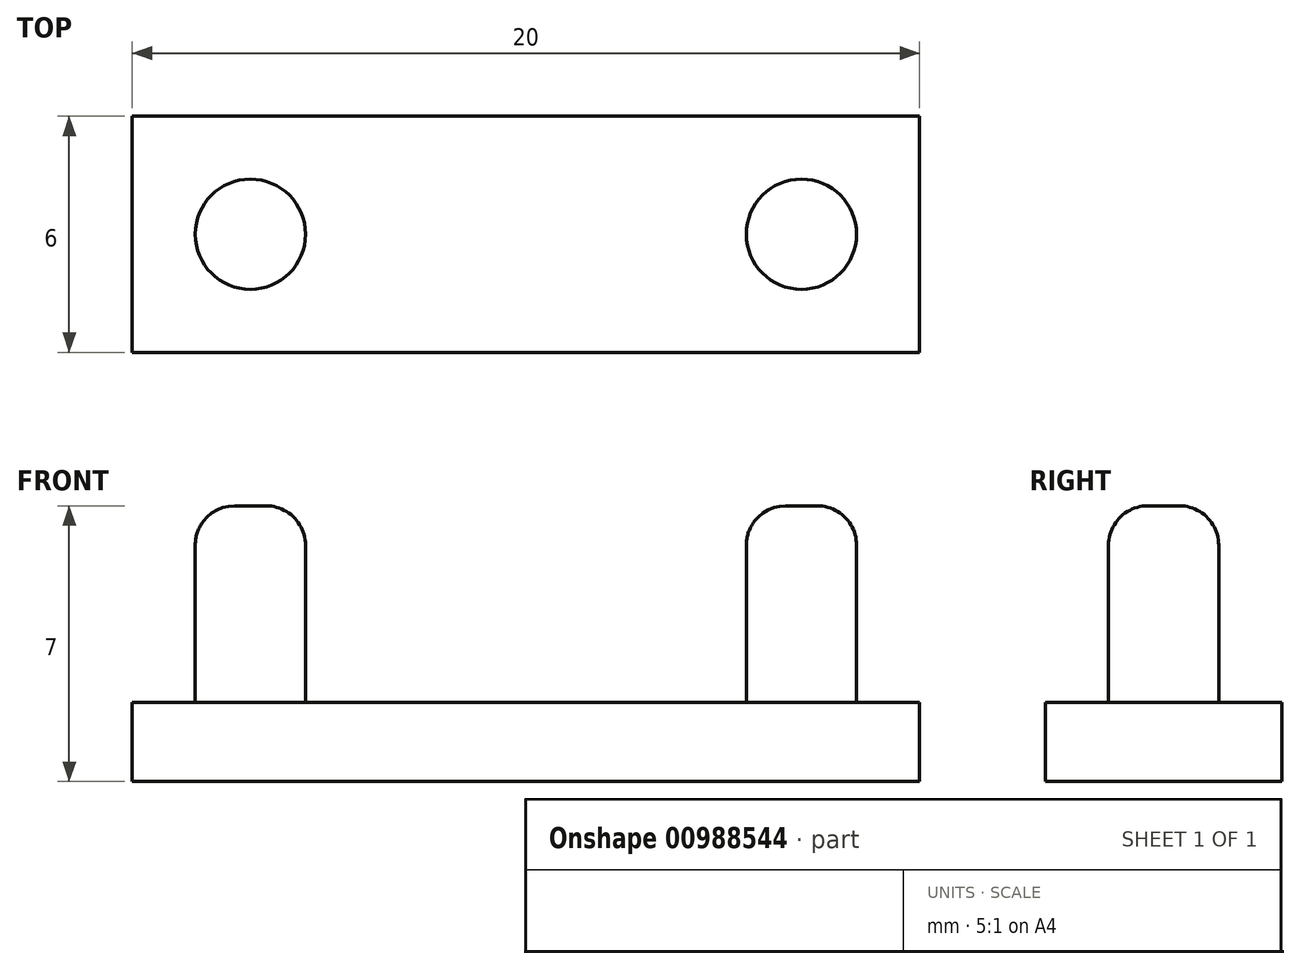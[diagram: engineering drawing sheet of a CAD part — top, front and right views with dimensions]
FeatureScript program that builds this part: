
annotation { "Feature Type Name" : "Feature", "Feature Type Description" : "" }
export const myFeature = defineFeature(function(context is Context, id is Id, definition is map)
    precondition{}
    {
        {
            var Q0;
            Q0=qCreatedBy(makeId("Top.planeOp"),FACE);
            var sketch = newSketch(context, id + "F0", { "sketchPlane" : qUnion([Q0])});
            skLineSegment(sketch, "E0.bottom", {"start": v(-10, 3) * mm, "end": v(10, 3) * mm});
            skLineSegment(sketch, "E0.top", {"start": v(-10, -3) * mm, "end": v(10, -3) * mm});
            skLineSegment(sketch, "E0.left", {"start": v(-10, 3) * mm, "end": v(-10, -3) * mm});
            skLineSegment(sketch, "E0.right", {"start": v(10, 3) * mm, "end": v(10, -3) * mm});
            skPoint(sketch, "E0.middle", {"position": v(0, 0) * mm});
            skPoint(sketch, "E1", {"position": v(-7, 0) * mm});
            skPoint(sketch, "E2", {"position": v(7, 0) * mm});
            skSolve(sketch);
        }
        {
            var Q0;
            Q0=makeQuery(id+"F0.imprint","IMPRINT",FACE,{"disambiguationData":[TD([[makeQuery(id+"F0.imprint","IMPRINT",EDGE,{"derivedFrom":sQuery(id+"F0.wireOp",EDGE,"E0.bottom")}),-1.0]])]});
            extrude(context, id + "F1", {"entities" : qUnion([Q0]), "depth" : 2 * mm, "offsetDistance" : 25 * mm});
        }
        {
            var Q0;
            Q0=makeQuery(id+"F1.opExtrude","CAP_FACE",FACE,{"disambiguationData":[OSD([sQuery(id+"F0.wireOp",EDGE,"E0.bottom"),sQuery(id+"F0.wireOp",EDGE,"E0.top"),sQuery(id+"F0.wireOp",EDGE,"E0.left"),sQuery(id+"F0.wireOp",EDGE,"E0.right")])],"isStart":false});
            var sketch = newSketch(context, id + "F2", { "sketchPlane" : qUnion([Q0])});
            skPoint(sketch, "E3", {"position": v(-7, 0) * mm});
            skPoint(sketch, "E4", {"position": v(7, 0) * mm});
            skCircle(sketch, "E5", {"center": v(-7, 0) * mm, "radius": 1.4 * mm});
            skCircle(sketch, "E6", {"center": v(7, 0) * mm, "radius": 1.4 * mm});
            skSolve(sketch);
        }
        {
            var Q0;
            Q0=makeQuery(id+"F2.imprint","IMPRINT",FACE,{"disambiguationData":[TD([[makeQuery(id+"F2.imprint","IMPRINT",EDGE,{"derivedFrom":sQuery(id+"F2.wireOp",EDGE,"E5")}),1.0]])]});
            var Q1;
            Q1=makeQuery(id+"F2.imprint","IMPRINT",FACE,{"disambiguationData":[TD([[makeQuery(id+"F2.imprint","IMPRINT",EDGE,{"derivedFrom":sQuery(id+"F2.wireOp",EDGE,"E6")}),1.0]])]});
            extrude(context, id + "F3", {"entities" : qUnion([Q0, Q1]), "operationType" : NewBodyOperationType.ADD, "depth" : 5 * mm, "offsetDistance" : 25 * mm});
        }
        {
            var Q0;
            Q0=makeQuery(id+"F3.opExtrude","CAP_EDGE",EDGE,{"disambiguationData":[OSD([sQuery(id+"F2.wireOp",EDGE,"E5")])],"isStart":false});
            var Q1;
            Q1=makeQuery(id+"F3.opExtrude","CAP_EDGE",EDGE,{"disambiguationData":[OSD([sQuery(id+"F2.wireOp",EDGE,"E6")])],"isStart":false});
            fillet(context, id + "F4", {"entities" : qUnion([Q0, Q1]), "radius" : 1 * mm, "tangentPropagation" : true, "allowEdgeOverflow" : false});
        }
    });
